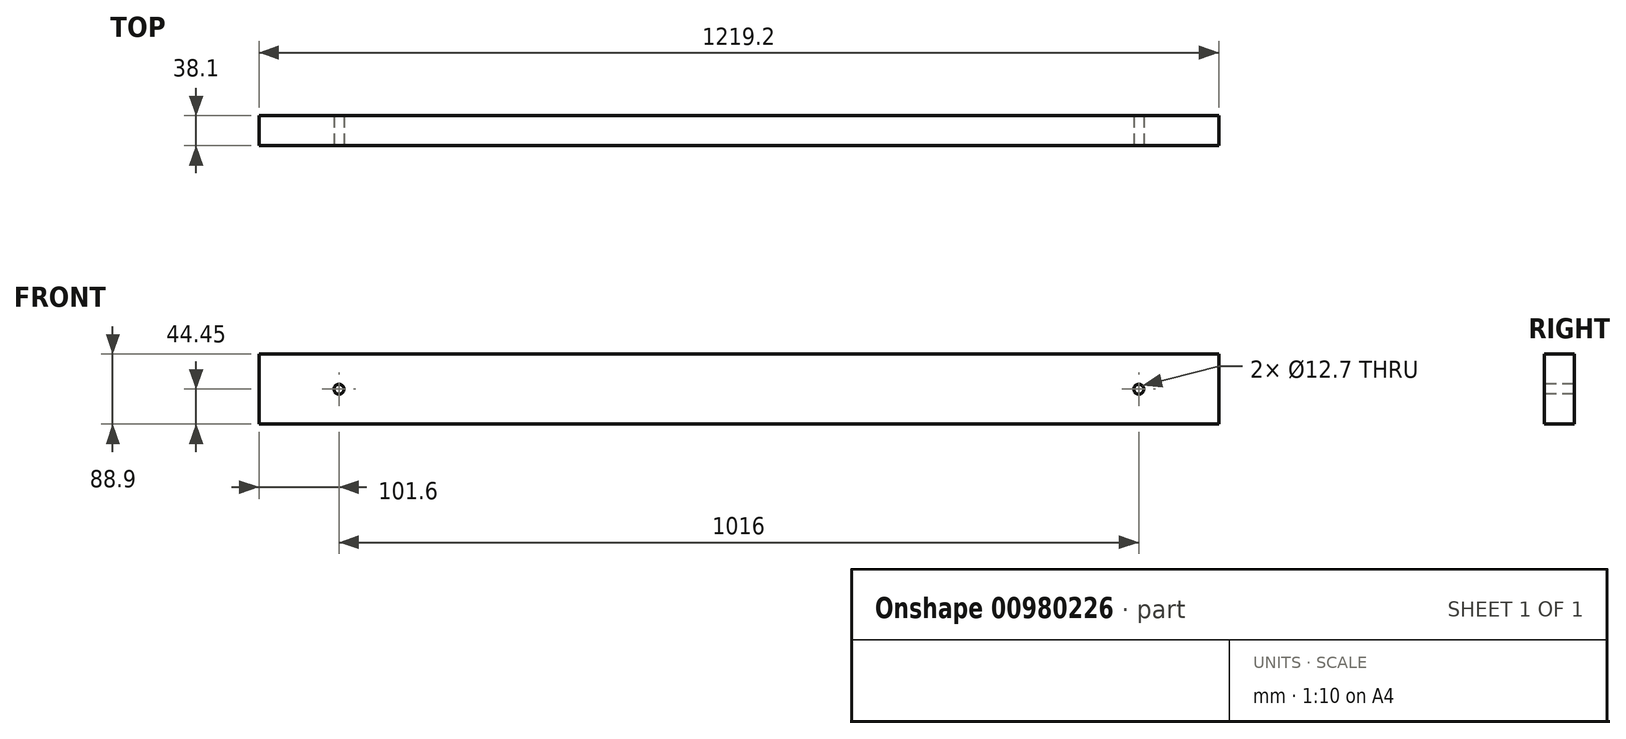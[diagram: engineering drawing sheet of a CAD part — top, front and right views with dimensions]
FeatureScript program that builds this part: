
annotation { "Feature Type Name" : "Feature", "Feature Type Description" : "" }
export const myFeature = defineFeature(function(context is Context, id is Id, definition is map)
    precondition{}
    {
        {
            var Q0;
            Q0=qCreatedBy(makeId("Right.planeOp"),FACE);
            var sketch = newSketch(context, id + "F0", { "sketchPlane" : qUnion([Q0])});
            skLineSegment(sketch, "E0.bottom", {"start": v(19.05, -44.45) * mm, "end": v(-19.05, -44.45) * mm});
            skLineSegment(sketch, "E0.top", {"start": v(19.05, 44.45) * mm, "end": v(-19.05, 44.45) * mm});
            skLineSegment(sketch, "E0.left", {"start": v(19.05, -44.45) * mm, "end": v(19.05, 44.45) * mm});
            skLineSegment(sketch, "E0.right", {"start": v(-19.05, -44.45) * mm, "end": v(-19.05, 44.45) * mm});
            skPoint(sketch, "E0.middle", {"position": v(0, 0) * mm});
            skSolve(sketch);
        }
        {
            var Q0;
            Q0 = qSketchRegion(id + "F0", true);
            extrude(context, id + "F1", {"entities" : qUnion([Q0]), "depth" : 1219.2 * mm, "offsetDistance" : 25.4 * mm});
        }
        {
            var Q0;
            Q0=makeQuery(id+"F1.opExtrude","SWEPT_FACE",FACE,{"disambiguationData":[OSD([sQuery(id+"F0.wireOp",EDGE,"E0.right")])]});
            var sketch = newSketch(context, id + "F2", { "sketchPlane" : qUnion([Q0])});
            skCircle(sketch, "E1", {"center": v(101.6, 0) * mm, "radius": 6.35 * mm});
            skSolve(sketch);
        }
        {
            var Q0;
            Q0 = qSketchRegion(id + "F2", true);
            extrude(context, id + "F3", {"entities" : qUnion([Q0]), "operationType" : NewBodyOperationType.REMOVE, "endBound" : BoundingType.THROUGH_ALL, "oppositeDirection" : true, "depth" : 25.4 * mm, "offsetDistance" : 25.4 * mm});
        }
        {
            var Q0;
            Q0=makeQuery(id+"F1.opExtrude","SWEPT_FACE",FACE,{"disambiguationData":[OSD([sQuery(id+"F0.wireOp",EDGE,"E0.right")])]});
            var sketch = newSketch(context, id + "F4", { "sketchPlane" : qUnion([Q0])});
            skCircle(sketch, "E2", {"center": v(1117.6, 0) * mm, "radius": 6.35 * mm});
            skPoint(sketch, "E2.centerSnap0", {"position": v(1219.2, 0) * mm});
            skSolve(sketch);
        }
        {
            var Q0;
            Q0 = qSketchRegion(id + "F4", true);
            extrude(context, id + "F5", {"entities" : qUnion([Q0]), "operationType" : NewBodyOperationType.REMOVE, "endBound" : BoundingType.THROUGH_ALL, "oppositeDirection" : true, "depth" : 25.4 * mm, "offsetDistance" : 25.4 * mm});
        }
    });
